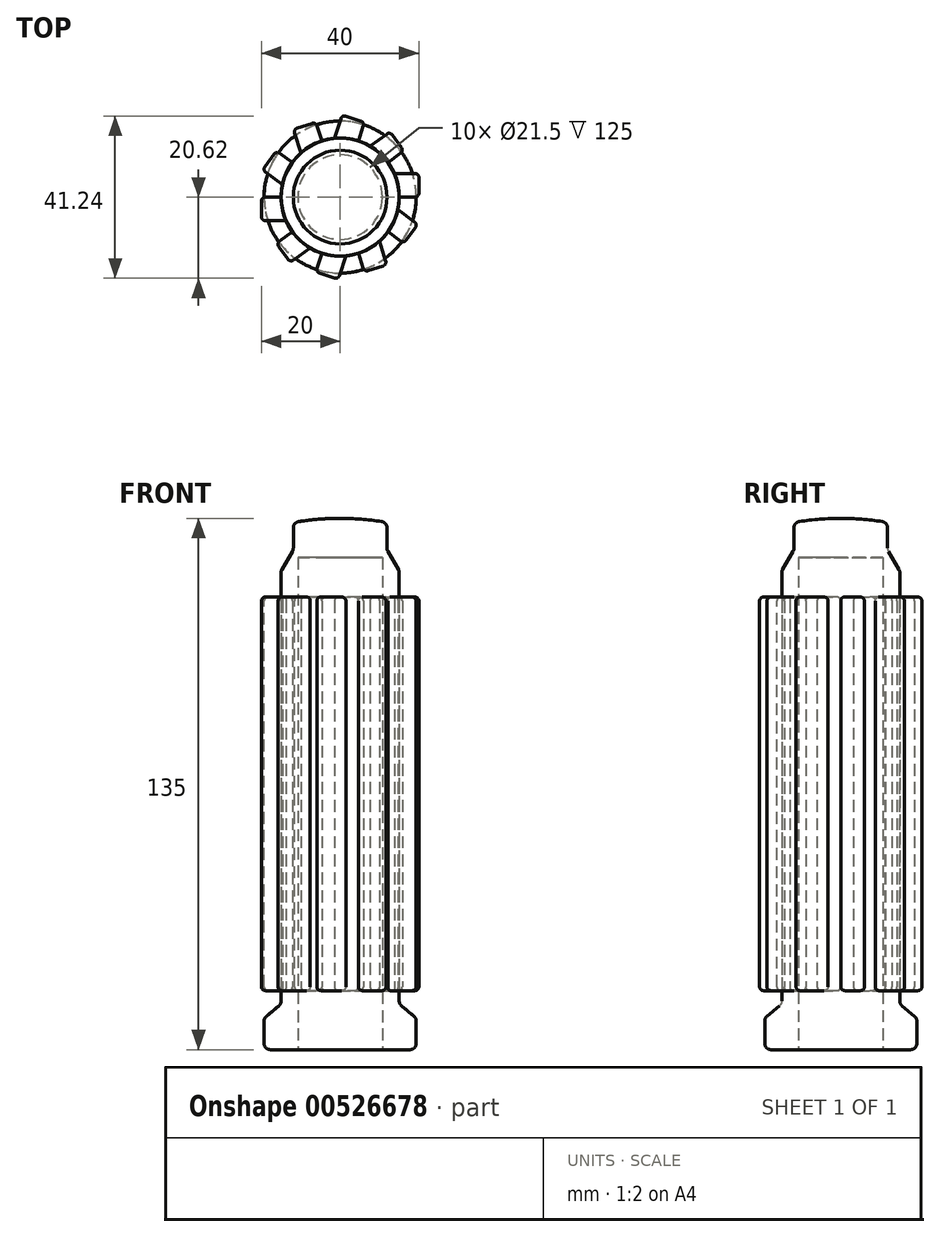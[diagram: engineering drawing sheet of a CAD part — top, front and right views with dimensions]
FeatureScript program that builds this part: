
annotation { "Feature Type Name" : "Feature", "Feature Type Description" : "" }
export const myFeature = defineFeature(function(context is Context, id is Id, definition is map)
    precondition{}
    {
        {
            var Q0;
            Q0=qCreatedBy(makeId("Front.planeOp"),FACE);
            var sketch = newSketch(context, id + "F0", { "sketchPlane" : qUnion([Q0])});
            skLineSegment(sketch, "E0", {"start": v(0, 135) * mm, "end": v(0, 125) * mm});
            skLineSegment(sketch, "E1", {"start": v(0, 125) * mm, "end": v(10.75, 125) * mm});
            skLineSegment(sketch, "E2", {"start": v(10.75, 125) * mm, "end": v(10.75, 0) * mm});
            skLineSegment(sketch, "E3", {"start": v(10.75, 0) * mm, "end": v(19.32, 0) * mm});
            skLineSegment(sketch, "E4", {"start": v(19.32, 0) * mm, "end": v(19.32, 8) * mm});
            skLineSegment(sketch, "E5", {"start": v(19.33, 8) * mm, "end": v(15, 11.63) * mm});
            skLineSegment(sketch, "E6", {"start": v(15, 11.63) * mm, "end": v(15, 121.63) * mm});
            skLineSegment(sketch, "E7", {"start": v(15, 121.63) * mm, "end": v(11.9, 127) * mm});
            skLineSegment(sketch, "E8", {"start": v(11.9, 127) * mm, "end": v(11.9, 133.95) * mm});
            skArc(sketch, "E9", {"start": v(11.9, 133.95) * mm, "mid": v(5.97, 134.74) * mm, "end": v(0, 135) * mm});
            skLineSegment(sketch, "E10", {"start": v(0, 0) * mm, "end": v(0, 125) * mm, "construction": true});
            skSolve(sketch);
        }
        {
            var Q0;
            Q0 = qSketchRegion(id + "F0", true);
            var Q1;
            Q1=sQuery(id+"F0.wireOp",EDGE,"E10");
            revolve(context, id + "F1", {"surfaceOperationType" : NewSurfaceOperationType.NEW, "entities" : qUnion([Q0]), "axis" : qUnion([Q1]), "revolveType" : RevolveType.FULL});
        }
        {
            var Q0;
            Q0=makeQuery(id+"F1.opRevolve","SWEPT_EDGE",EDGE,{"disambiguationData":[OSD([sQuery(id+"F0.wireOp",EDGE,"E7"),sQuery(id+"F0.wireOp",EDGE,"E8")])]});
            var Q1;
            Q1=makeQuery(id+"F1.opRevolve","SWEPT_EDGE",EDGE,{"disambiguationData":[OSD([sQuery(id+"F0.wireOp",EDGE,"E8"),sQuery(id+"F0.wireOp",EDGE,"E9")])]});
            var Q2;
            Q2=makeQuery(id+"F1.opRevolve","SWEPT_EDGE",EDGE,{"disambiguationData":[OSD([sQuery(id+"F0.wireOp",EDGE,"E6"),sQuery(id+"F0.wireOp",EDGE,"E7")])]});
            var Q3;
            Q3=makeQuery(id+"F1.opRevolve","SWEPT_EDGE",EDGE,{"disambiguationData":[OSD([sQuery(id+"F0.wireOp",EDGE,"E5"),sQuery(id+"F0.wireOp",EDGE,"E6")])]});
            var Q4;
            Q4=makeQuery(id+"F1.opRevolve","SWEPT_EDGE",EDGE,{"disambiguationData":[OSD([sQuery(id+"F0.wireOp",EDGE,"E4"),sQuery(id+"F0.wireOp",EDGE,"E5")])]});
            var Q5;
            Q5=makeQuery(id+"F1.opRevolve","SWEPT_EDGE",EDGE,{"disambiguationData":[OSD([sQuery(id+"F0.wireOp",EDGE,"E3"),sQuery(id+"F0.wireOp",EDGE,"E4")])]});
            fillet(context, id + "F2", {"entities" : qUnion([Q0, Q1, Q2, Q3, Q4, Q5]), "radius" : 1.6 * mm, "tangentPropagation" : true, "allowEdgeOverflow" : false});
        }
        {
            var Q0;
            Q0=qCreatedBy(makeId("Right.planeOp"),FACE);
            cPlane(context, id + "F3", {"entities" : qUnion([Q0]), "cplaneType" : CPlaneType.OFFSET, "offset" : 20 * mm, "width" : 150 * mm, "height" : 150 * mm});
        }
        {
            var Q0;
            Q0=qCreatedBy(id+"F3.planeOp",FACE);
            var sketch = newSketch(context, id + "F4", { "sketchPlane" : qUnion([Q0])});
            skLineSegment(sketch, "E11.bottom", {"start": v(0, 15) * mm, "end": v(6, 15) * mm});
            skLineSegment(sketch, "E11.top", {"start": v(0, 115) * mm, "end": v(6, 115) * mm});
            skLineSegment(sketch, "E11.left", {"start": v(0, 15) * mm, "end": v(0, 115) * mm});
            skLineSegment(sketch, "E11.right", {"start": v(6, 15) * mm, "end": v(6, 115) * mm});
            skSolve(sketch);
        }
        {
            var Q0;
            Q0 = qSketchRegion(id + "F4", true);
            var Q1;
            Q1=makeQuery(id+"F1.opRevolve","SWEPT_FACE",FACE,{"disambiguationData":[OSD([sQuery(id+"F0.wireOp",EDGE,"E6")])]});
            extrude(context, id + "F5", {"entities" : qUnion([Q0]), "endBound" : BoundingType.UP_TO_SURFACE, "oppositeDirection" : true, "depth" : 25 * mm, "endBoundEntityFace" : qUnion([Q1]), "offsetDistance" : 25 * mm});
        }
        {
            var Q0;
            Q0=makeQuery(id+"F5.opExtrude","CAP_FACE",FACE,{"disambiguationData":[OSD([sQuery(id+"F4.wireOp",EDGE,"E11.bottom"),sQuery(id+"F4.wireOp",EDGE,"E11.top"),sQuery(id+"F4.wireOp",EDGE,"E11.left"),sQuery(id+"F4.wireOp",EDGE,"E11.right")])],"isStart":true});
            var Q1;
            Q1=makeQuery(id+"F5.opExtrude","TWEAK_EDGE",EDGE,{"derivedFrom":[makeQuery(id+"F1.opRevolve","SWEPT_FACE",FACE,{"disambiguationData":[OSD([sQuery(id+"F0.wireOp",EDGE,"E6")])]}),makeQuery(id+"F4.imprint","IMPRINT",EDGE,{"derivedFrom":sQuery(id+"F4.wireOp",EDGE,"E11.left")})]});
            var Q2;
            Q2=makeQuery(id+"F5.opExtrude","CAP_EDGE",EDGE,{"disambiguationData":[OSD([sQuery(id+"F4.wireOp",EDGE,"E11.top")])],"isStart":true});
            var Q3;
            Q3=makeQuery(id+"F5.opExtrude","CAP_EDGE",EDGE,{"disambiguationData":[OSD([sQuery(id+"F4.wireOp",EDGE,"E11.left")])],"isStart":true});
            var Q4;
            Q4=makeQuery(id+"F5.opExtrude","TWEAK_EDGE",EDGE,{"derivedFrom":[makeQuery(id+"F1.opRevolve","SWEPT_FACE",FACE,{"disambiguationData":[OSD([sQuery(id+"F0.wireOp",EDGE,"E6")])]}),makeQuery(id+"F4.imprint","IMPRINT",EDGE,{"derivedFrom":sQuery(id+"F4.wireOp",EDGE,"E11.top")})]});
            var Q5;
            Q5=makeQuery(id+"F5.opExtrude","TWEAK_EDGE",EDGE,{"derivedFrom":[makeQuery(id+"F1.opRevolve","SWEPT_FACE",FACE,{"disambiguationData":[OSD([sQuery(id+"F0.wireOp",EDGE,"E6")])]}),makeQuery(id+"F4.imprint","IMPRINT",EDGE,{"derivedFrom":sQuery(id+"F4.wireOp",EDGE,"E11.right")})]});
            var Q6;
            Q6=makeQuery(id+"F5.opExtrude","CAP_EDGE",EDGE,{"disambiguationData":[OSD([sQuery(id+"F4.wireOp",EDGE,"E11.bottom")])],"isStart":true});
            var Q7;
            Q7=makeQuery(id+"F5.opExtrude","TWEAK_EDGE",EDGE,{"derivedFrom":[makeQuery(id+"F1.opRevolve","SWEPT_FACE",FACE,{"disambiguationData":[OSD([sQuery(id+"F0.wireOp",EDGE,"E6")])]}),makeQuery(id+"F4.imprint","IMPRINT",EDGE,{"derivedFrom":sQuery(id+"F4.wireOp",EDGE,"E11.bottom")})]});
            var Q8;
            Q8=makeQuery(id+"F5.opExtrude","SWEPT_EDGE",EDGE,{"disambiguationData":[OSD([sQuery(id+"F4.wireOp",EDGE,"E11.top"),sQuery(id+"F4.wireOp",EDGE,"E11.left")])]});
            var Q9;
            Q9=makeQuery(id+"F5.opExtrude","SWEPT_EDGE",EDGE,{"disambiguationData":[OSD([sQuery(id+"F4.wireOp",EDGE,"E11.bottom"),sQuery(id+"F4.wireOp",EDGE,"E11.left")])]});
            var Q10;
            Q10=makeQuery(id+"F5.opExtrude","SWEPT_EDGE",EDGE,{"disambiguationData":[OSD([sQuery(id+"F4.wireOp",EDGE,"E11.top"),sQuery(id+"F4.wireOp",EDGE,"E11.right")])]});
            var Q11;
            Q11=makeQuery(id+"F5.opExtrude","SWEPT_EDGE",EDGE,{"disambiguationData":[OSD([sQuery(id+"F4.wireOp",EDGE,"E11.bottom"),sQuery(id+"F4.wireOp",EDGE,"E11.right")])]});
            var Q12;
            Q12=makeQuery(id+"F5.opExtrude","CAP_EDGE",EDGE,{"disambiguationData":[OSD([sQuery(id+"F4.wireOp",EDGE,"E11.right")])],"isStart":true});
            fillet(context, id + "F6", {"entities" : qUnion([Q0, Q1, Q2, Q3, Q4, Q5, Q6, Q7, Q8, Q9, Q10, Q11, Q12]), "radius" : 1 * mm, "tangentPropagation" : true, "allowEdgeOverflow" : false});
        }
        {
            var Q0;
            Q0=makeQuery(id+"F1.opRevolve","SWEPT_BODY",BODY,{"disambiguationData":[OSD([sQuery(id+"F0.wireOp",EDGE,"E0"),sQuery(id+"F0.wireOp",EDGE,"E1"),sQuery(id+"F0.wireOp",EDGE,"E2"),sQuery(id+"F0.wireOp",EDGE,"E3"),sQuery(id+"F0.wireOp",EDGE,"E4"),sQuery(id+"F0.wireOp",EDGE,"E5"),sQuery(id+"F0.wireOp",EDGE,"E6"),sQuery(id+"F0.wireOp",EDGE,"E7"),sQuery(id+"F0.wireOp",EDGE,"E8"),sQuery(id+"F0.wireOp",EDGE,"E9")])]});
            var Q1;
            Q1=makeQuery(id+"F5.opExtrude","SWEPT_BODY",BODY,{"disambiguationData":[OSD([sQuery(id+"F4.wireOp",EDGE,"E11.bottom"),sQuery(id+"F4.wireOp",EDGE,"E11.top"),sQuery(id+"F4.wireOp",EDGE,"E11.left"),sQuery(id+"F4.wireOp",EDGE,"E11.right")])]});
            var Q2;
            Q2=sQuery(id+"F0.wireOp",EDGE,"E10");
            circularPattern(context, id + "F7", {"entities" : qUnion([Q0, Q1]), "axis" : qUnion([Q2]), "angle" : 360 * degree, "instanceCount" : 10, "oppositeDirection" : true, "equalSpace" : true});
        }
    });
